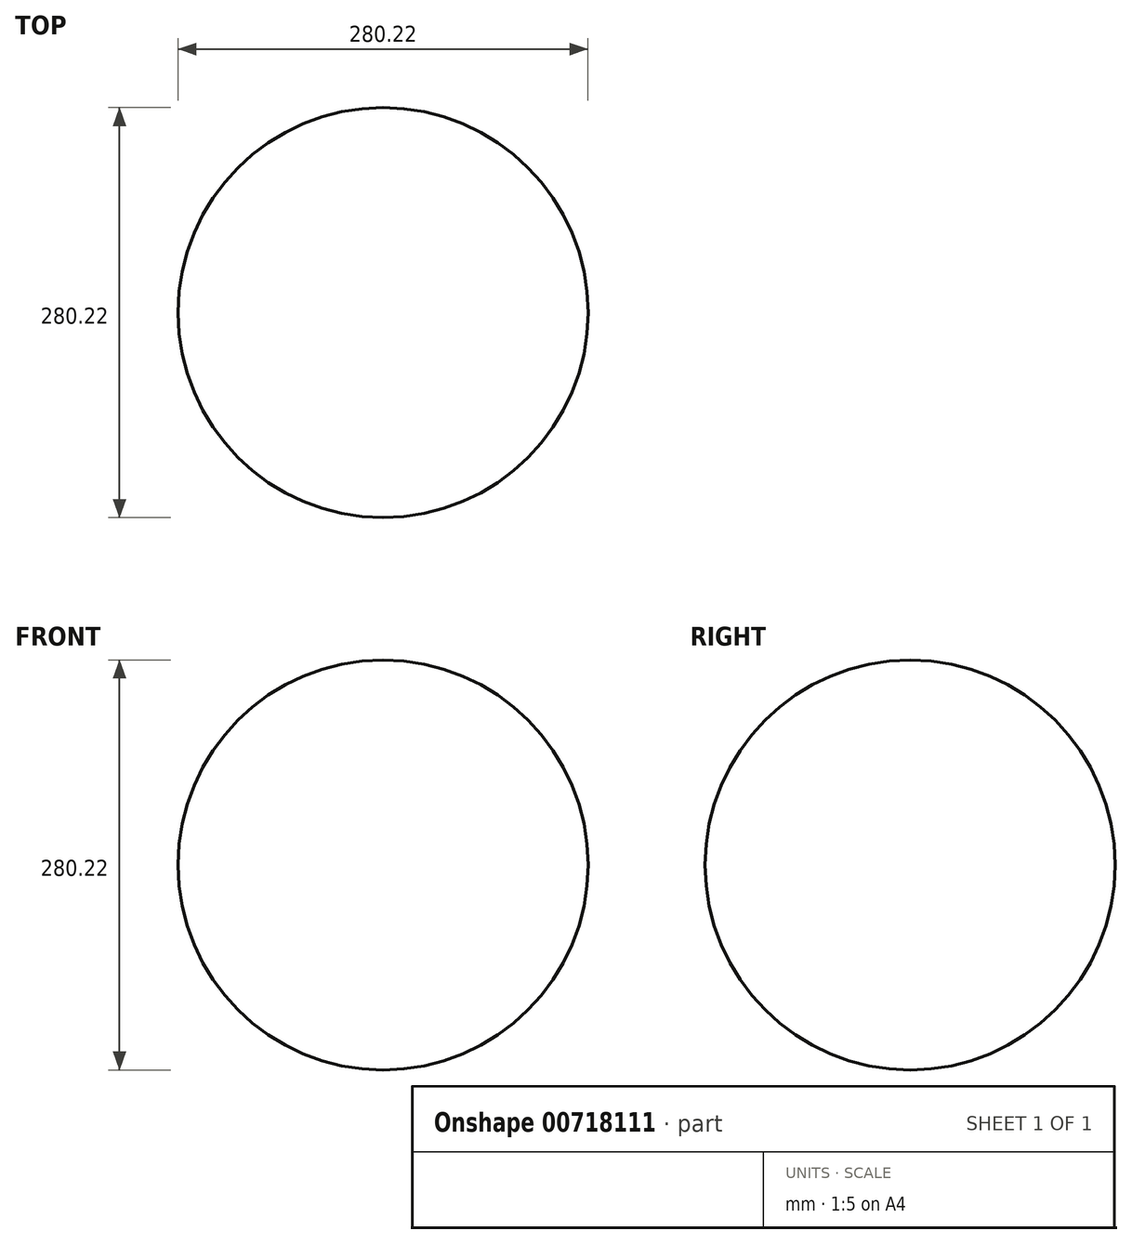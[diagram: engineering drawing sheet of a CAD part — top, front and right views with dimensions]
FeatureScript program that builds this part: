
annotation { "Feature Type Name" : "Feature", "Feature Type Description" : "" }
export const myFeature = defineFeature(function(context is Context, id is Id, definition is map)
    precondition{}
    {
        {
            var Q0;
            Q0=qCreatedBy(makeId("Top.planeOp"),FACE);
            var sketch = newSketch(context, id + "F0", { "sketchPlane" : qUnion([Q0])});
            skCircle(sketch, "E0", {"center": v(0, 0) * mm, "radius": 140.11 * mm});
            skLineSegment(sketch, "E1", {"start": v(0, 140.11) * mm, "end": v(0, -140.11) * mm});
            skSolve(sketch);
        }
        {
            var Q0;
            {var subQ0=sQuery(id+"F0.wireOp",EDGE,"E1");Q0=makeQuery(id+"F0.imprint","IMPRINT",FACE,{"disambiguationData":[TD([[makeQuery(id+"F0.imprint","IMPRINT",EDGE,{"derivedFrom":subQ0}),1.0]])]});}
            var Q1;
            Q1=sQuery(id+"F0.wireOp",EDGE,"E1");
            revolve(context, id + "F1", {"surfaceOperationType" : NewSurfaceOperationType.NEW, "entities" : qUnion([Q0]), "axis" : qUnion([Q1]), "revolveType" : RevolveType.FULL});
        }
    });
